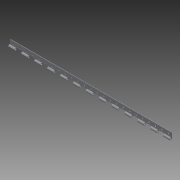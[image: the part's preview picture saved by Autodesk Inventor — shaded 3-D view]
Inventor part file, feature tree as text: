
AUTODESK INVENTOR PART (.ipt)
format: ipt  version: 2015 SP1 (Build 190203100, 203)  size: 169,472 bytes
history: native  units: in
note: dims shown in document units (in); Inventor stores cm internally (conversion verified against a paired STEP export)
features: sketch x4, extrude x3, pattern_linear x2, hole x1, plane x1, projected_geometry x1
ambient origin geometry x8: Origin, YZ Plane, XZ Plane, XY Plane, X Axis, Y Axis, Z Axis, Center Point
bodies: Solid1 (feature_tree)
feature tree (12):
  extrude  "Extrusion1"  Depth=0.0625in
  extrude  "Extrusion2"  Depth=0.1875in
  hole  "Hole1"  [1 undecoded]
  pattern_linear  "Rectangular Pattern2"  Spacing1=25.0in  [1 undecoded]
  plane  "Work Plane1"
  extrude  "Extrusion4"  Depth=2.0in
  pattern_linear  "Rectangular Pattern3"  Spacing1=0.5in  [1 undecoded]
  sketch  "Sketch1"  dims[d0=1.0in d1=0.0625in]
  sketch  "Sketch2"  dims[d2=0.375in d3=0.1875in]
  sketch  "Sketch4"  dims[d4=0.125in d5=25.0in d6=0.0in]
  sketch  "Sketch5"  dims[d7=0.25in d8=25.0in d9=0.0in d15=0.375in d16=0.5in d17=0.25in d18=0.75in d19=0.375in d20=0.25in d21=0.5635in d22=1.0in d23=0.8108in d24=9.8425in d26=1.0in d27=-1.0in d28=1.0in d29=0.0in d30=4.7244in d32=2.0in]
  projected_geometry  "Projected Loop1"
note: 3 required parameter values undecoded (feature->parameter linkage not recoverable at this tier; creation-order binding heuristic only, values carry confidence <= 0.55)
